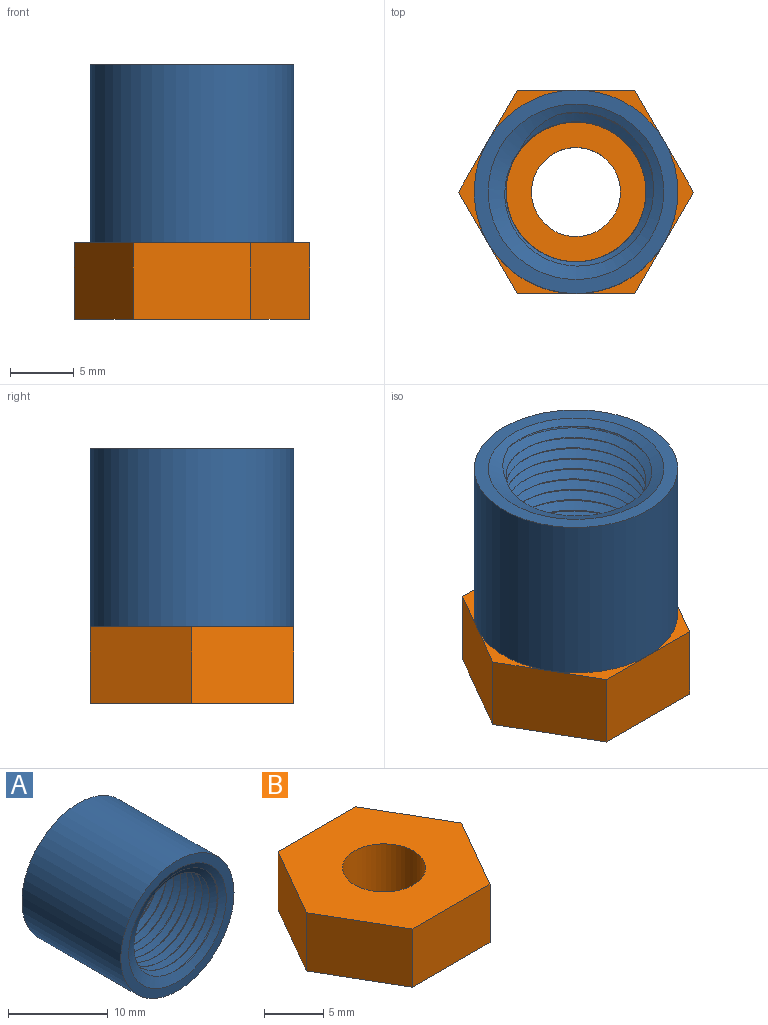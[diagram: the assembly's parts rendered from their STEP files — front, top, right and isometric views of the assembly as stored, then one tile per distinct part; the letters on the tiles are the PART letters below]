
ASSEMBLY  parts=2 mates=1
PART A: 8 faces, bbox 16.5x15.2x16.5 mm
  f0: bspline ~14.68x14.5mm, area 405.8mm2, adj f1,f3,f6,f7
  f1: cylinder r=5.5mm len=13.4mm, axis (0,-1,0), area 34.5mm2, adj f0,f2,f6,f7
  f2: bspline ~14.68x14.66mm, area 407.3mm2, adj f1,f3,f6,f7
  f3: bspline ~14.08x12.74mm, area 112.6mm2, adj f0,f2,f6,f7
  f4: plane 16x16mm, normal (0,-1,0), area 51.6mm2, adj f5,f7
  f5: cylinder r=8mm len=16mm, axis (0,-1,0), area 703.7mm2, adj f4,f6
  f6: plane 16.5x16.5mm, normal (0,1,0), area 90.9mm2, adj f0,f1,f2,f3,f5
  f7: cone r=5.17mm half-angle=66.7deg, axis (0,-1,0), area 43.1mm2, adj f0,f1,f2,f3,f4
PART B: 10 faces, bbox 18.5x16x6 mm
  f0: plane 8x6mm, normal (-0.87,0.5,0), area 55.4mm2, adj f1,f6,f7,f8
  f1: plane 8x6mm, normal (-0.87,-0.5,0), area 55.4mm2, adj f0,f2,f7,f8
  f2: plane 9.24x6mm, normal (0,-1,0), area 55.4mm2, adj f1,f3,f7,f8
  f3: plane 8x6mm, normal (0.87,-0.5,0), area 55.4mm2, adj f2,f4,f7,f8
  f4: plane 8x6mm, normal (0.87,0.5,0), area 55.4mm2, adj f3,f6,f7,f8
  f5: cylinder r=3.5mm len=7mm, axis (0,0,-1), area 110mm2, adj f7,f9
  f6: plane 9.24x6mm, normal (0,1,0), area 55.4mm2, adj f0,f4,f7,f8
  f7: plane 18.48x16mm, normal (0,0,1), area 183.2mm2, adj f0,f1,f2,f3,f4,f5,f6
  f8: plane 18.48x16mm, normal (0,0,-1), area 158.1mm2, adj f0,f1,f2,f3,f4,f6,f9
  f9: cone r=4.5mm half-angle=45deg, axis (0,0,-1), area 35.5mm2, adj f5,f8
PLACE A rot(axis=(-1,0,0),90deg) t=(13.63,7.99,7.59)mm
PLACE B t=(13.63,7.99,-12.41)mm
MATE fastened A.f1 <-> B.f5  axis (0,0,-1) through (13.63,7.99,-6.41)mm
